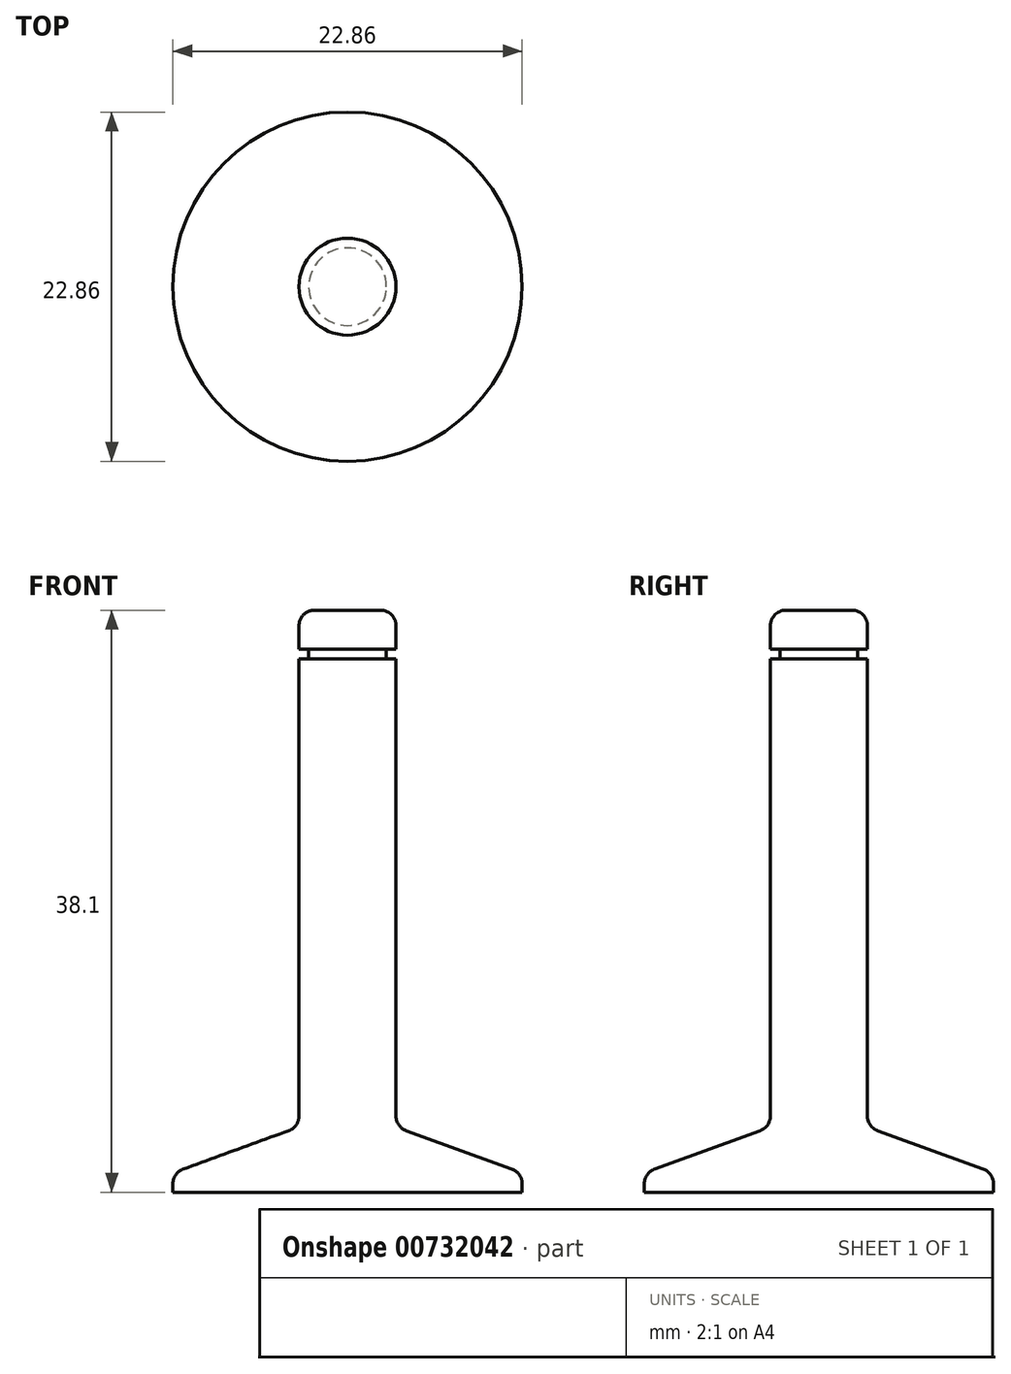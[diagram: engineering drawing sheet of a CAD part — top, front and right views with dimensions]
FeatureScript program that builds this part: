
annotation { "Feature Type Name" : "Feature", "Feature Type Description" : "" }
export const myFeature = defineFeature(function(context is Context, id is Id, definition is map)
    precondition{}
    {
        {
            var Q0;
            Q0=qCreatedBy(makeId("Front.planeOp"),FACE);
            var sketch = newSketch(context, id + "F0", { "sketchPlane" : qUnion([Q0])});
            skLineSegment(sketch, "E0", {"start": v(0, 0) * mm, "end": v(11.43, 0) * mm});
            skLineSegment(sketch, "E1", {"start": v(11.43, 0) * mm, "end": v(11.43, 1.27) * mm});
            skLineSegment(sketch, "E2", {"start": v(11.43, 1.27) * mm, "end": v(3.18, 4.27) * mm});
            skLineSegment(sketch, "E3", {"start": v(3.18, 4.27) * mm, "end": v(3.18, 38.1) * mm});
            skLineSegment(sketch, "E4", {"start": v(3.18, 38.1) * mm, "end": v(0, 38.1) * mm});
            skLineSegment(sketch, "E5", {"start": v(0, 38.1) * mm, "end": v(0, 0) * mm});
            skSolve(sketch);
        }
        {
            var Q0;
            Q0=makeQuery(id+"F0.imprint","IMPRINT",FACE,{"disambiguationData":[TD([[makeQuery(id+"F0.imprint","IMPRINT",EDGE,{"derivedFrom":sQuery(id+"F0.wireOp",EDGE,"E0")}),1.0]])]});
            var Q1;
            Q1=sQuery(id+"F0.wireOp",EDGE,"E5");
            revolve(context, id + "F1", {"surfaceOperationType" : NewSurfaceOperationType.NEW, "entities" : qUnion([Q0]), "axis" : qUnion([Q1]), "revolveType" : RevolveType.FULL});
        }
        {
            var Q0;
            Q0=makeQuery(id+"F1.opRevolve","SWEPT_EDGE",EDGE,{"disambiguationData":[OSD([sQuery(id+"F0.wireOp",EDGE,"E1"),sQuery(id+"F0.wireOp",EDGE,"E2")])]});
            var Q1;
            Q1=makeQuery(id+"F1.opRevolve","SWEPT_EDGE",EDGE,{"disambiguationData":[OSD([sQuery(id+"F0.wireOp",EDGE,"E2"),sQuery(id+"F0.wireOp",EDGE,"E3")])]});
            fillet(context, id + "F2", {"entities" : qUnion([Q0, Q1]), "radius" : 1.02 * mm, "tangentPropagation" : true, "allowEdgeOverflow" : false});
        }
        {
            var Q0;
            Q0=qCreatedBy(makeId("Front.planeOp"),FACE);
            var sketch = newSketch(context, id + "F3", { "sketchPlane" : qUnion([Q0])});
            skLineSegment(sketch, "E6.bottom", {"start": v(3.18, 35.56) * mm, "end": v(2.54, 35.56) * mm});
            skLineSegment(sketch, "E6.top", {"start": v(3.18, 34.92) * mm, "end": v(2.54, 34.92) * mm});
            skLineSegment(sketch, "E6.right", {"start": v(3.18, 35.56) * mm, "end": v(3.18, 34.92) * mm});
            skLineSegment(sketch, "E7", {"start": v(2.54, 35.56) * mm, "end": v(2.54, 34.92) * mm});
            skSolve(sketch);
        }
        {
            var Q0;
            Q0 = qSketchRegion(id + "F3", true);
            var Q1;
            Q1=makeQuery(id+"F1.opRevolve","SWEPT_FACE",FACE,{"disambiguationData":[OSD([sQuery(id+"F0.wireOp",EDGE,"E3")])]});
            revolve(context, id + "F4", {"operationType" : NewBodyOperationType.REMOVE, "surfaceOperationType" : NewSurfaceOperationType.NEW, "entities" : qUnion([Q0]), "axis" : qUnion([Q1]), "revolveType" : RevolveType.FULL, "oppositeDirection" : true});
        }
        {
            var Q0;
            Q0=makeQuery(id+"F1.opRevolve","SWEPT_EDGE",EDGE,{"disambiguationData":[OSD([sQuery(id+"F0.wireOp",EDGE,"E3"),sQuery(id+"F0.wireOp",EDGE,"E4")])]});
            fillet(context, id + "F5", {"entities" : qUnion([Q0]), "radius" : 1.02 * mm, "tangentPropagation" : true, "allowEdgeOverflow" : false});
        }
    });
